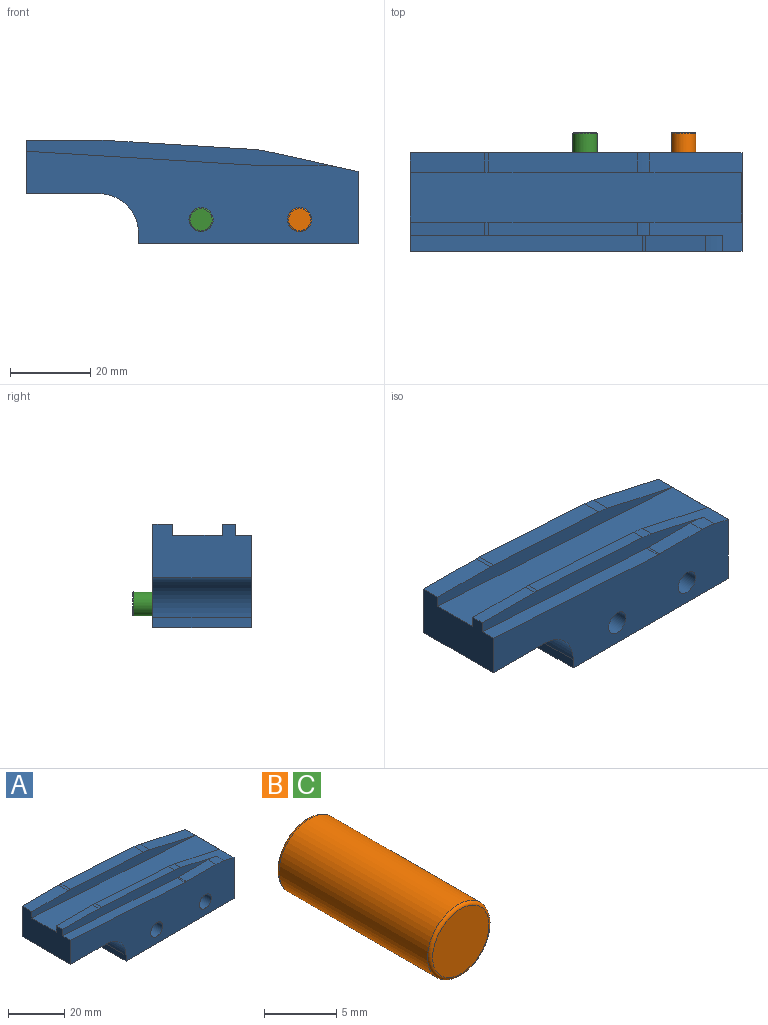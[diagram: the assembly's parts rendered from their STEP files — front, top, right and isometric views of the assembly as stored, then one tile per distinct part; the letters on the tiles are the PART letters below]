
ASSEMBLY  parts=3 mates=2
PART A: 31 faces, bbox 82.5x24.5x25.8 mm
  f0: plane 24.5x22.87mm, normal (0.22,0,0.98), area 212.7mm2, adj f5,f11,f12,f13,f15,f16,f17,f19
  f1: plane 18.39x3.25mm, normal (0,0,1), area 59.8mm2, adj f2,f13,f16,f23
  f2: plane 24.5x13.25mm, normal (-1,0,0), area 279.9mm2, adj f1,f5,f6,f7,f12,f13,f14,f15
  f3: plane 36.91x4.95mm, normal (0.06,0,1), area 183.1mm2, adj f12,f15,f20,f22
  f4: plane 36.91x3.25mm, normal (0.06,0,1), area 120.2mm2, adj f13,f16,f21,f23
  f5: plane 82.5x23.01mm, normal (0,-1,0), area 1318.5mm2, adj f0,f2,f7,f8,f9,f10,f11,f14
  f6: plane 18.39x4.95mm, normal (0,0,1), area 91mm2, adj f2,f12,f15,f22
  f7: plane 24.5x18mm, normal (0,0,-1), area 441mm2, adj f2,f5,f8,f12
  f8: cylinder r=10mm len=24.5mm, axis (0,1,0), area 384.8mm2, adj f5,f7,f9,f12
  f9: plane 24.5x2.5mm, normal (-1,0,0), area 61.2mm2, adj f5,f8,f10,f12
  f10: plane 54.5x24.5mm, normal (0,0,-1), area 1335.2mm2, adj f5,f9,f11,f12
  f11: plane 24.5x17.95mm, normal (1,0,0), area 439.8mm2, adj f0,f5,f10,f12
  f12: plane 82.5x25.75mm, normal (0,1,0), area 1528.8mm2, adj f0,f2,f3,f6,f7,f8,f9,f10
  f13: plane 77.64x6.72mm, normal (0,-1,0), area 249.6mm2, adj f0,f1,f2,f4,f14,f18,f19,f21
  f14: plane 57.85x4mm, normal (0.06,0,1), area 231.8mm2, adj f2,f5,f13,f24
  f15: plane 82.44x7.79mm, normal (0,-1,0), area 263.5mm2, adj f0,f2,f3,f6,f17,f20,f22
  f16: plane 82.44x7.79mm, normal (0,1,0), area 263.5mm2, adj f0,f1,f2,f4,f17,f21,f23
  f17: plane 82.44x12.3mm, normal (0.06,0,1), area 1016mm2, adj f0,f2,f15,f16
  f18: plane 14.88x4mm, normal (0,0,1), area 59.5mm2, adj f5,f13,f19,f24
  f19: cylinder r=20mm len=4.33mm, axis (0,1,0), area 17.4mm2, adj f0,f5,f13,f18
  f20: cylinder r=20mm len=4.95mm, axis (0,1,0), area 15.5mm2, adj f0,f3,f12,f15
  f21: cylinder r=20mm len=3.25mm, axis (0,1,0), area 10.2mm2, adj f0,f4,f13,f16
  f22: cylinder r=20mm len=4.95mm, axis (0,1,0), area 6mm2, adj f3,f6,f12,f15
  f23: cylinder r=20mm len=3.25mm, axis (0,1,0), area 4mm2, adj f1,f4,f13,f16
  f24: cylinder r=5mm len=4mm, axis (0,-1,0), area 2.3mm2, adj f5,f13,f14,f18
  f25: cylinder r=3mm len=24.5mm, axis (0,1,0), area 461.8mm2, adj f5,f12
  f26: cylinder r=3mm len=24.5mm, axis (0,1,0), area 461.8mm2, adj f5,f12
  f27: cone r=0mm half-angle=59deg, axis (0,1,0), area 22.9mm2, adj f28
  f28: cylinder r=2.5mm len=20mm, axis (0,1,0), area 314.2mm2, adj f12,f27
  f29: cone r=0mm half-angle=59deg, axis (0,1,0), area 22.9mm2, adj f30
  f30: cylinder r=2.5mm len=20mm, axis (0,1,0), area 314.2mm2, adj f12,f29
PART B: 5 faces, bbox 6.5x15x6.5 mm
  f0: cylinder r=3mm len=14.5mm, axis (0,1,0), area 273.3mm2, adj f3,f4
  f1: plane 5.5x5.5mm, normal (0,-1,0), area 23.8mm2, adj f4
  f2: plane 5.5x5.5mm, normal (0,1,0), area 23.8mm2, adj f3
  f3: torus R=2.75mm, axis (0,-1,0), area 7.2mm2, adj f0,f2
  f4: torus R=2.75mm, axis (0,-1,0), area 7.2mm2, adj f0,f1
PART C: same geometry as B
PLACE A t=(-3.87,1.2,9.63)mm
PLACE B t=(-18.37,6.2,15.63)mm
PLACE C t=(-42.87,6.2,15.63)mm
MATE fastened C.f0 <-> A.f26  axis (0,1,0) through (-42.87,6.2,15.63)mm
MATE fastened B.f0 <-> A.f25  axis (0,1,0) through (-18.37,6.2,15.63)mm
